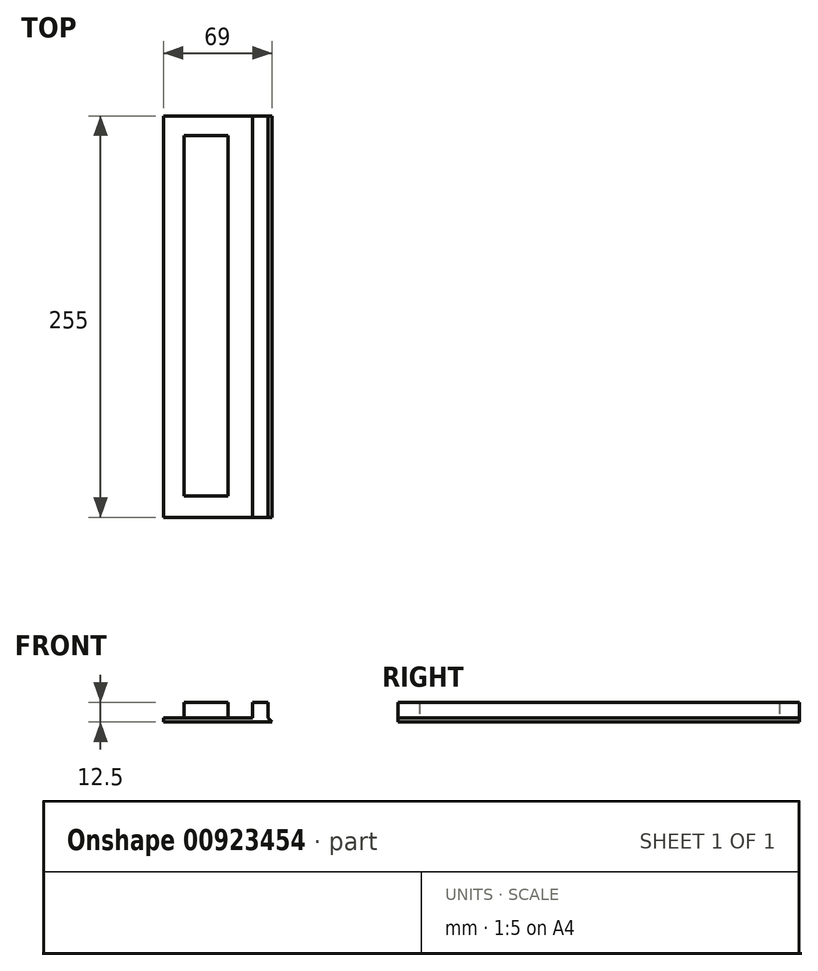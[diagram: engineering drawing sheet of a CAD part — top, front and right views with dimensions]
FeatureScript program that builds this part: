
annotation { "Feature Type Name" : "Feature", "Feature Type Description" : "" }
export const myFeature = defineFeature(function(context is Context, id is Id, definition is map)
    precondition{}
    {
        {
            var Q0;
            Q0=qCreatedBy(makeId("Top.planeOp"),FACE);
            var sketch = newSketch(context, id + "F0", { "sketchPlane" : qUnion([Q0])});
            skLineSegment(sketch, "E0.bottom", {"start": v(34.5, -127.5) * mm, "end": v(-34.5, -127.5) * mm});
            skLineSegment(sketch, "E0.top", {"start": v(34.5, 127.5) * mm, "end": v(-34.5, 127.5) * mm});
            skLineSegment(sketch, "E0.left", {"start": v(34.5, -127.5) * mm, "end": v(34.5, 127.5) * mm});
            skLineSegment(sketch, "E0.right", {"start": v(-34.5, -127.5) * mm, "end": v(-34.5, 127.5) * mm});
            skPoint(sketch, "E0.middle", {"position": v(0, 0) * mm});
            skSolve(sketch);
        }
        {
            var Q0;
            Q0=makeQuery(id+"F0.imprint","IMPRINT",FACE,{"disambiguationData":[TD([[makeQuery(id+"F0.imprint","IMPRINT",EDGE,{"derivedFrom":sQuery(id+"F0.wireOp",EDGE,"E0.bottom")}),-1.0]])]});
            extrude(context, id + "F1", {"entities" : qUnion([Q0]), "depth" : 2.5 * mm, "offsetDistance" : 25 * mm});
        }
        {
            var Q0;
            Q0=makeQuery(id+"F1.opExtrude","CAP_EDGE",EDGE,{"disambiguationData":[OSD([sQuery(id+"F0.wireOp",EDGE,"E0.left")])],"isStart":false});
            chamfer(context, id + "F2", {"entities" : qUnion([Q0]), "width" : 2.5 * mm, "tangentPropagation" : true});
        }
        {
            var Q0;
            Q0=makeQuery(id+"F1.opExtrude","CAP_FACE",FACE,{"disambiguationData":[OSD([sQuery(id+"F0.wireOp",EDGE,"E0.bottom"),sQuery(id+"F0.wireOp",EDGE,"E0.top"),sQuery(id+"F0.wireOp",EDGE,"E0.left"),sQuery(id+"F0.wireOp",EDGE,"E0.right")])],"isStart":false});
            var sketch = newSketch(context, id + "F3", { "sketchPlane" : qUnion([Q0])});
            skLineSegment(sketch, "E1.bottom", {"start": v(32, 127.5) * mm, "end": v(22, 127.5) * mm});
            skLineSegment(sketch, "E1.top", {"start": v(32, -127.5) * mm, "end": v(22, -127.5) * mm});
            skLineSegment(sketch, "E1.left", {"start": v(32, 127.5) * mm, "end": v(32, -127.5) * mm});
            skLineSegment(sketch, "E1.right", {"start": v(22, 127.5) * mm, "end": v(22, -127.5) * mm});
            skSolve(sketch);
        }
        {
            var Q0;
            Q0=makeQuery(id+"F3.imprint","IMPRINT",FACE,{"disambiguationData":[TD([[makeQuery(id+"F3.imprint","IMPRINT",EDGE,{"derivedFrom":sQuery(id+"F3.wireOp",EDGE,"E1.bottom")}),1.0]])]});
            extrude(context, id + "F4", {"entities" : qUnion([Q0]), "operationType" : NewBodyOperationType.ADD, "depth" : 10 * mm, "offsetDistance" : 25 * mm});
        }
        {
            var Q0;
            Q0=makeQuery(id+"F1.opExtrude","CAP_FACE",FACE,{"disambiguationData":[OSD([sQuery(id+"F0.wireOp",EDGE,"E0.bottom"),sQuery(id+"F0.wireOp",EDGE,"E0.top"),sQuery(id+"F0.wireOp",EDGE,"E0.left"),sQuery(id+"F0.wireOp",EDGE,"E0.right")])],"isStart":false});
            var sketch = newSketch(context, id + "F5", { "sketchPlane" : qUnion([Q0])});
            skLineSegment(sketch, "E2.bottom", {"start": v(-21.35, 114.86) * mm, "end": v(6.67, 114.86) * mm});
            skLineSegment(sketch, "E2.top", {"start": v(-21.35, -113.77) * mm, "end": v(6.67, -113.77) * mm});
            skLineSegment(sketch, "E2.left", {"start": v(-21.35, 114.86) * mm, "end": v(-21.35, -113.77) * mm});
            skLineSegment(sketch, "E2.right", {"start": v(6.67, 114.86) * mm, "end": v(6.67, -113.77) * mm});
            skSolve(sketch);
        }
        {
            var Q0;
            Q0=makeQuery(id+"F5.imprint","IMPRINT",FACE,{"disambiguationData":[TD([[makeQuery(id+"F5.imprint","IMPRINT",EDGE,{"derivedFrom":sQuery(id+"F5.wireOp",EDGE,"E2.bottom")}),-1.0]])]});
            extrude(context, id + "F6", {"entities" : qUnion([Q0]), "operationType" : NewBodyOperationType.ADD, "depth" : 10 * mm, "offsetDistance" : 25 * mm});
        }
    });
